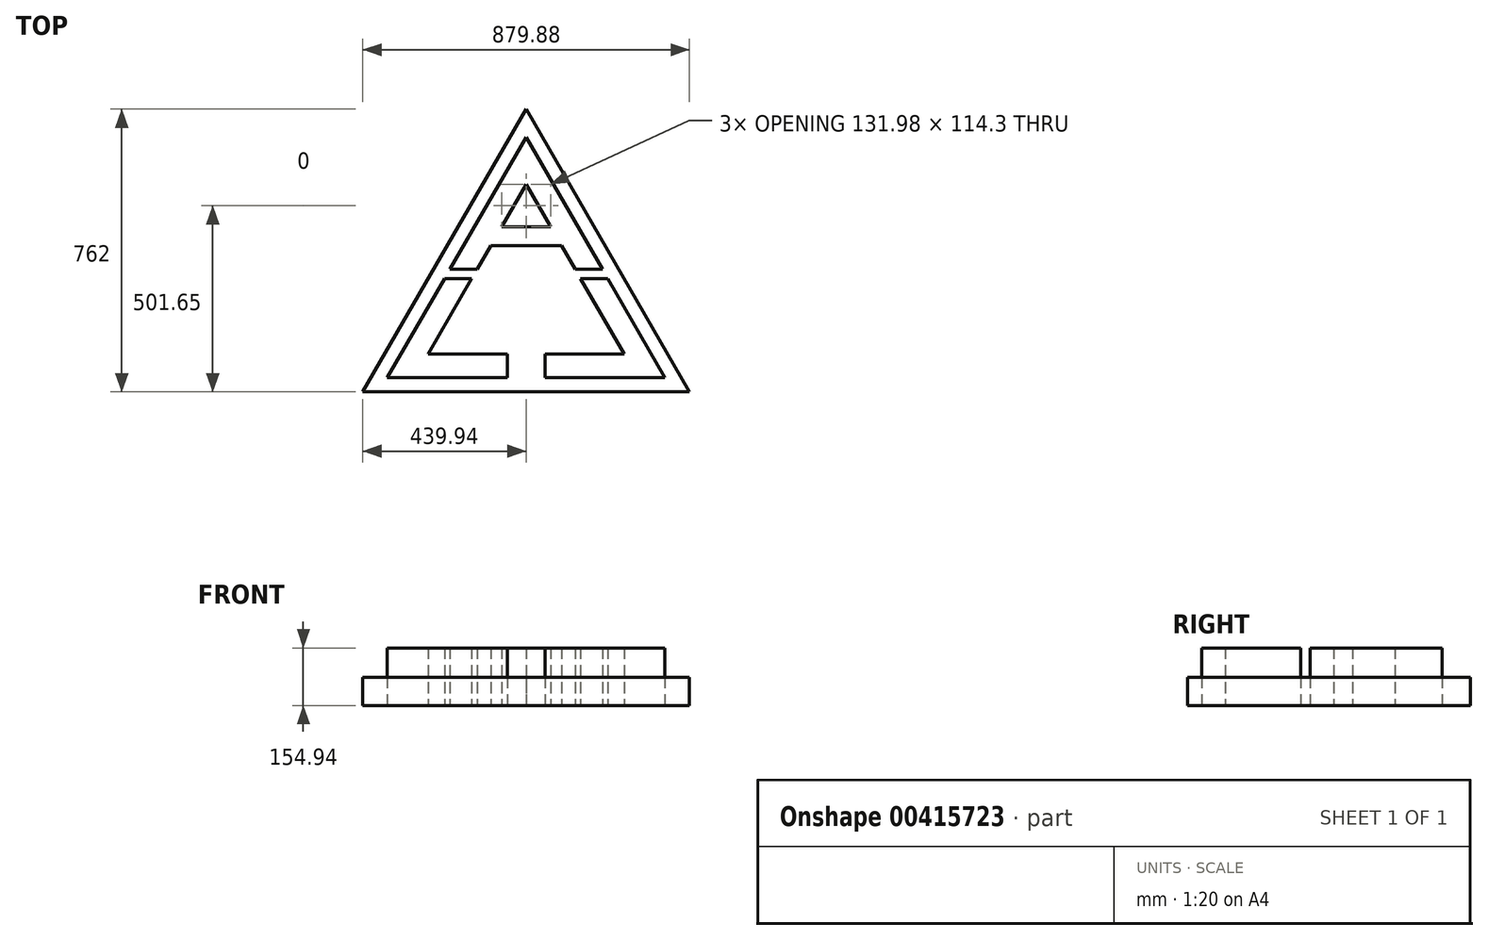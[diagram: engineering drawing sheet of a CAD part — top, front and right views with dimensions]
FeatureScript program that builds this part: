
annotation { "Feature Type Name" : "Feature", "Feature Type Description" : "" }
export const myFeature = defineFeature(function(context is Context, id is Id, definition is map)
    precondition{}
    {
        {
            var Q0;
            Q0=qCreatedBy(makeId("Top.planeOp"),FACE);
            var sketch = newSketch(context, id + "F0", { "sketchPlane" : qUnion([Q0])});
            skArc(sketch, "E0", {"start": v(381.51, -152.8) * mm, "mid": v(355.91, 205.49) * mm, "end": v(58.43, 406.8) * mm});
            skLineSegment(sketch, "E1", {"start": v(0, 508) * mm, "end": v(-439.94, -254) * mm});
            skLineSegment(sketch, "E2", {"start": v(-439.94, -254) * mm, "end": v(439.94, -254) * mm});
            skLineSegment(sketch, "E3", {"start": v(0, 508) * mm, "end": v(439.94, -254) * mm});
            skLineSegment(sketch, "E4", {"start": v(-219.97, 50.8) * mm, "end": v(-373.95, -215.9) * mm});
            skLineSegment(sketch, "E5", {"start": v(-373.95, -215.9) * mm, "end": v(-50.8, -215.9) * mm});
            skLineSegment(sketch, "E6", {"start": v(205.3, 76.2) * mm, "end": v(0, 431.8) * mm});
            skLineSegment(sketch, "E7", {"start": v(0, 431.8) * mm, "end": v(-205.3, 76.2) * mm});
            skLineSegment(sketch, "E8", {"start": v(66, 190.5) * mm, "end": v(-66, 190.5) * mm});
            skLineSegment(sketch, "E9", {"start": v(-439.94, -254) * mm, "end": v(-11.6, -254) * mm});
            skLineSegment(sketch, "E10", {"start": v(0, 508) * mm, "end": v(-214.17, 137.05) * mm});
            skLineSegment(sketch, "E11", {"start": v(0, 508) * mm, "end": v(219.97, 127) * mm});
            skLineSegment(sketch, "E12", {"start": v(-219.97, 127) * mm, "end": v(-439.94, -254) * mm});
            skLineSegment(sketch, "E13", {"start": v(225.77, 116.95) * mm, "end": v(439.94, -254) * mm});
            skLineSegment(sketch, "E14", {"start": v(0, -254) * mm, "end": v(439.94, -254) * mm});
            skLineSegment(sketch, "E15", {"start": v(439.94, -254) * mm, "end": v(0, 508) * mm});
            skLineSegment(sketch, "E16", {"start": v(131.98, 76.2) * mm, "end": v(205.3, 76.2) * mm});
            skArc(sketch, "E17", {"start": v(-323.08, -254) * mm, "mid": v(0, -410.97) * mm, "end": v(323.08, -254) * mm});
            skArc(sketch, "E18", {"start": v(-58.43, 406.8) * mm, "mid": v(-355.91, 205.49) * mm, "end": v(-381.51, -152.8) * mm});
            skLineSegment(sketch, "E19", {"start": v(-219.97, 50.8) * mm, "end": v(-146.65, 50.8) * mm});
            skLineSegment(sketch, "E20", {"start": v(-146.65, 50.8) * mm, "end": v(-263.96, -152.4) * mm});
            skLineSegment(sketch, "E21", {"start": v(-263.96, -152.4) * mm, "end": v(-50.8, -152.4) * mm});
            skLineSegment(sketch, "E22", {"start": v(-50.8, -152.4) * mm, "end": v(-50.8, -215.9) * mm});
            skLineSegment(sketch, "E23", {"start": v(219.97, 50.8) * mm, "end": v(373.95, -215.9) * mm});
            skLineSegment(sketch, "E24", {"start": v(373.95, -215.9) * mm, "end": v(50.8, -215.9) * mm});
            skLineSegment(sketch, "E25", {"start": v(219.97, 50.8) * mm, "end": v(146.65, 50.8) * mm});
            skLineSegment(sketch, "E26", {"start": v(146.65, 50.8) * mm, "end": v(263.96, -152.4) * mm});
            skLineSegment(sketch, "E27", {"start": v(263.96, -152.4) * mm, "end": v(50.8, -152.4) * mm});
            skLineSegment(sketch, "E28", {"start": v(50.8, -152.4) * mm, "end": v(50.8, -215.9) * mm});
            skLineSegment(sketch, "E29", {"start": v(131.98, 76.2) * mm, "end": v(95.32, 139.7) * mm});
            skLineSegment(sketch, "E30", {"start": v(95.32, 139.7) * mm, "end": v(-95.32, 139.7) * mm});
            skLineSegment(sketch, "E31", {"start": v(0, 304.8) * mm, "end": v(-66, 190.5) * mm});
            skLineSegment(sketch, "E32", {"start": v(-131.98, 76.2) * mm, "end": v(-205.3, 76.2) * mm});
            skLineSegment(sketch, "E33", {"start": v(66, 190.5) * mm, "end": v(0, 304.8) * mm});
            skLineSegment(sketch, "E34", {"start": v(-95.32, 139.7) * mm, "end": v(-131.98, 76.2) * mm});
            skSolve(sketch);
        }
        {
            var Q0;
            Q0=makeQuery(id+"F0.imprint","IMPRINT",FACE,{"disambiguationData":[TD([[makeQuery(id+"F0.imprint","IMPRINT",EDGE,{"derivedFrom":sQuery(id+"F0.wireOp",EDGE,"E6")}),1.0]])]});
            var Q1;
            Q1=makeQuery(id+"F0.imprint","IMPRINT",FACE,{"disambiguationData":[TD([[makeQuery(id+"F0.imprint","IMPRINT",EDGE,{"derivedFrom":sQuery(id+"F0.wireOp",EDGE,"E4")}),1.0]])]});
            var Q2;
            Q2=makeQuery(id+"F0.imprint","IMPRINT",FACE,{"disambiguationData":[TD([[makeQuery(id+"F0.imprint","IMPRINT",EDGE,{"derivedFrom":sQuery(id+"F0.wireOp",EDGE,"E23")}),-1.0]])]});
            extrude(context, id + "F1", {"entities" : qUnion([Q0, Q1, Q2]), "depth" : 154.94 * mm});
        }
        {
            var Q0;
            Q0=makeQuery(id+"F0.imprint","IMPRINT",FACE,{"disambiguationData":[TD([[makeQuery(id+"F0.imprint","IMPRINT",EDGE,{"derivedFrom":sQuery(id+"F0.wireOp",EDGE,"E4")}),-1.0]])]});
            var Q1;
            Q1=makeQuery(id+"F0.imprint","IMPRINT",FACE,{"disambiguationData":[TD([[makeQuery(id+"F0.imprint","IMPRINT",EDGE,{"derivedFrom":sQuery(id+"F0.wireOp",EDGE,"E8")}),-1.0]])]});
            var Q2;
            Q2=makeQuery(id+"F0.imprint","IMPRINT",FACE,{"disambiguationData":[TD([[makeQuery(id+"F0.imprint","IMPRINT",EDGE,{"derivedFrom":sQuery(id+"F0.wireOp",EDGE,"E23")}),-1.0]])]});
            var Q3;
            Q3=makeQuery(id+"F0.imprint","IMPRINT",FACE,{"disambiguationData":[TD([[makeQuery(id+"F0.imprint","IMPRINT",EDGE,{"derivedFrom":sQuery(id+"F0.wireOp",EDGE,"E4")}),1.0]])]});
            var Q4;
            Q4=makeQuery(id+"F0.imprint","IMPRINT",FACE,{"disambiguationData":[TD([[makeQuery(id+"F0.imprint","IMPRINT",EDGE,{"derivedFrom":sQuery(id+"F0.wireOp",EDGE,"E6")}),1.0]])]});
            extrude(context, id + "F2", {"entities" : qUnion([Q0, Q1, Q2, Q3, Q4]), "depth" : 76.2 * mm});
        }
    });
